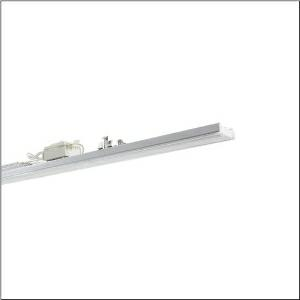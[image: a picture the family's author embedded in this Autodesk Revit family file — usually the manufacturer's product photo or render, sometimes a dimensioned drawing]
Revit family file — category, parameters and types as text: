
# Revit family: licross_r__11_recessed_mo_51te12dv4fxg3s_1d5e
name_source: partatom
category: Lighting Fixtures
units: mm (PartAtom-declared; Revit-internal decimal feet)

## family parameters
Cut with Voids When Loaded = No
Host = Face
Light Source = No
Part Type = Normal
Room Calculation Point = No
Round Connector Dimension = Use Diameter
Shared = No

## types (1)
- --- (1 x LED, 1010 lm, 5.5 W, 4000K)
    Apparent Load = 6 VA
    CIE Flux Codes = 67 92 99 100 100
    Color Rendering = 80
    Color Temperature = 4000K
    Default Elevation = 1800 mm
    Description = Licross® 11 Recessed MO, luminaire insert, of sheet steel, galvanised, coil coated, white, length: 2.250mm, width: 66mm, height: 67mm, LED rated luminous flux: 15.360lm, light colour: 840, control gear: DALI 2 (for two DALI lines), with plug, 6-pole, with phase selection, for trunking rail, 14-core, mains connection: 220..240V, AC, 50/60Hz, rated input power: 88W, for trunking rail, 14-core, halogen-free wiring, for emergency light function, converter,control gear: single battery element, battery: LiFePO4, 9Ah, primary optical cover: cover, of PMMA, light emission: direct distribution, primary light characteristic: symmetric, protection rating (complete): IP54, insulation class (complete): insulation class I (protective earthing), certification: CE, UKCA, protection symbol: D if used in an environment with non-conductive dust loads with corresponding accessories, impact resistance: IK06, permissible ambient temperature for indoor applications: +5..+35°C, standard: EN 60598-2-22, LABS conformity tested according to VDMA 24364:2018-05, reducing of maximum allowable ambient temperature of 5°C with ceiling mounting, corresponds to IFS (International Featured Standards) requirements for safety and quality in the food industry, packaging unit: 1 piece
    Height = 58 mm
    Lamp = 1 x LED
    Lamp Light Flux = 1010 lm
    Lamp Power = 5.5 W
    Lamp count = 1
    Length = 2250 mm
    Luminous efficacy = 184 lm/W
    Manufacturer = Siteco
    ModVariant = No
    Model = 51TE12DV4FXG3S
    Mounting Place = Ceiling
    Mounting Type = Pendant
    Number of Poles = 1
    OnlyDefault = Yes
    Power Factor = 1
    Product Name = Licross® 11 Recessed MO
    Product group = luminaire insert
    ProductGroupID = 902
    Protection Class = Protection class I
    Protection Degree = IP 54
    RLX_Detail_Level = 1
    RLX_Emergency_Light_Flux = 0 lm
    RLX_Emergency_Type = 0
    RLX_Emergency_Type_DB = No
    RlxData = <blob elided: 29841 chars, md5=380ba1f2>
    Socket = socket
    Standby Power = 0 W
    System Light Flux = 1010 lm
    System Power = 6 W
    Type Comments = : emergency light operation: 3 h
    Type Image = l_1296930.jpg
    URL = http://relux.com
    VarID = @adj_085282
    Voltage = 0 V
    Weight = 0.00 kg
    Width = 66 mm

## geometry (parser evidence)
native form markers: Blend x4, Sweep x10
no freeform markers — native parametric forms only
